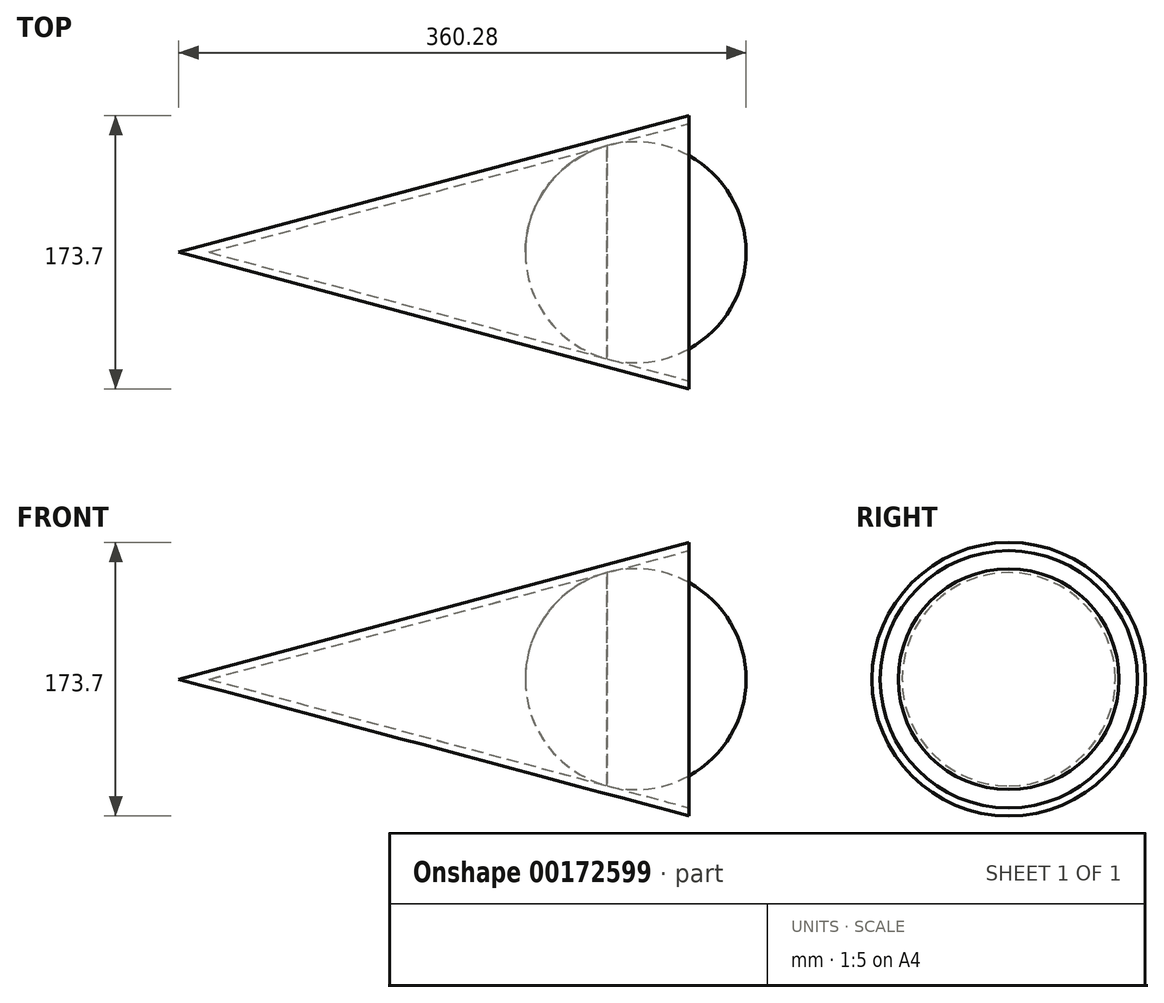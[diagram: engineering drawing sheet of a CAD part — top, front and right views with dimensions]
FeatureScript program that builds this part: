
annotation { "Feature Type Name" : "Feature", "Feature Type Description" : "" }
export const myFeature = defineFeature(function(context is Context, id is Id, definition is map)
    precondition{}
    {
        {
            var Q0;
            Q0=qCreatedBy(makeId("Top.planeOp"),FACE);
            var sketch = newSketch(context, id + "F0", { "sketchPlane" : qUnion([Q0])});
            skLineSegment(sketch, "E0", {"start": v(33.94, 0) * mm, "end": v(33.94, 81.67) * mm});
            skLineSegment(sketch, "E1", {"start": v(33.94, 0) * mm, "end": v(-270.86, 0) * mm});
            skLineSegment(sketch, "E2", {"start": v(-270.86, 0) * mm, "end": v(33.94, 81.67) * mm});
            skLineSegment(sketch, "E3", {"start": v(0, 0) * mm, "end": v(-18.14, 67.72) * mm, "construction": true});
            skLineSegment(sketch, "E4", {"start": v(-18.14, 0) * mm, "end": v(-18.14, 67.72) * mm, "construction": true});
            skArc(sketch, "E5", {"start": v(-18.14, 67.72) * mm, "mid": v(-55.62, 42.68) * mm, "end": v(-70.1, 0) * mm});
            skArc(sketch, "E6", {"start": v(-18.14, 67.72) * mm, "mid": v(42.68, 55.62) * mm, "end": v(70.1, 0) * mm});
            skLineSegment(sketch, "E7", {"start": v(70.1, 0) * mm, "end": v(-70.1, 0) * mm, "construction": true});
            skLineSegment(sketch, "E8.0", {"start": v(-272.16, 4.83) * mm, "end": v(32.64, 86.5) * mm});
            skLineSegment(sketch, "E9", {"start": v(70.1, 0) * mm, "end": v(-70.1, 0) * mm});
            skLineSegment(sketch, "E10", {"start": v(-272.16, 4.83) * mm, "end": v(-290.18, 0) * mm});
            skLineSegment(sketch, "E11", {"start": v(-290.18, 0) * mm, "end": v(-270.86, 0) * mm});
            skLineSegment(sketch, "E12", {"start": v(33.94, 81.67) * mm, "end": v(33.94, 86.85) * mm});
            skLineSegment(sketch, "E13", {"start": v(32.64, 86.5) * mm, "end": v(33.94, 86.85) * mm});
            skSolve(sketch);
        }
        {
            var Q0;
            {var subQ5=sQuery(id+"F0.wireOp",EDGE,"E5");Q0=makeQuery(id+"F0.imprint","IMPRINT",FACE,{"disambiguationData":[TD([[makeQuery(id+"F0.imprint","IMPRINT",EDGE,{"derivedFrom":subQ5}),1.0]])]});}
            var Q1;
            Q1=sQuery(id+"F0.wireOp",EDGE,"E1");
            revolve(context, id + "F1", {"entities" : qUnion([Q0]), "axis" : qUnion([Q1]), "revolveType" : RevolveType.FULL});
        }
        {
            var Q0;
            {var subQ0=sQuery(id+"F0.wireOp",EDGE,"E9");var subQ1=sQuery(id+"F0.wireOp",EDGE,"E0");var subQ2=makeQuery(id+"F0.imprint","INTERSECT",VERTEX,{"derivedFrom":[subQ1,subQ0]});Q0=makeQuery(id+"F0.imprint","IMPRINT",FACE,{"disambiguationData":[TD([[makeQuery(id+"F0.imprint","IMPRINT",EDGE,{"disambiguationData":[TD([[subQ2,-1.0]])],"derivedFrom":subQ1}),-1.0]])]});}
            var Q1;
            Q1=sQuery(id+"F0.wireOp",EDGE,"E1");
            revolve(context, id + "F2", {"operationType" : NewBodyOperationType.ADD, "entities" : qUnion([Q0]), "axis" : qUnion([Q1]), "revolveType" : RevolveType.FULL});
        }
        {
            var Q0;
            Q0=makeQuery(id+"F0.imprint","IMPRINT",FACE,{"disambiguationData":[TD([[makeQuery(id+"F0.imprint","IMPRINT",EDGE,{"derivedFrom":sQuery(id+"F0.wireOp",EDGE,"E8.0")}),-1.0]])]});
            var Q1;
            Q1=sQuery(id+"F0.wireOp",EDGE,"E1");
            revolve(context, id + "F3", {"entities" : qUnion([Q0]), "axis" : qUnion([Q1]), "revolveType" : RevolveType.FULL});
        }
        {
            var Q0;
            {var subQ0=sQuery(id+"F0.wireOp",EDGE,"E1");Q0=makeQuery(id+"F0.imprint","IMPRINT",FACE,{"disambiguationData":[TD([[makeQuery(id+"F0.imprint","IMPRINT",EDGE,{"derivedFrom":subQ0}),-1.0]])]});}
            var Q1;
            Q1=sQuery(id+"F0.wireOp",EDGE,"E1");
            revolve(context, id + "F4", {"entities" : qUnion([Q0]), "axis" : qUnion([Q1]), "revolveType" : RevolveType.FULL});
        }
    });
